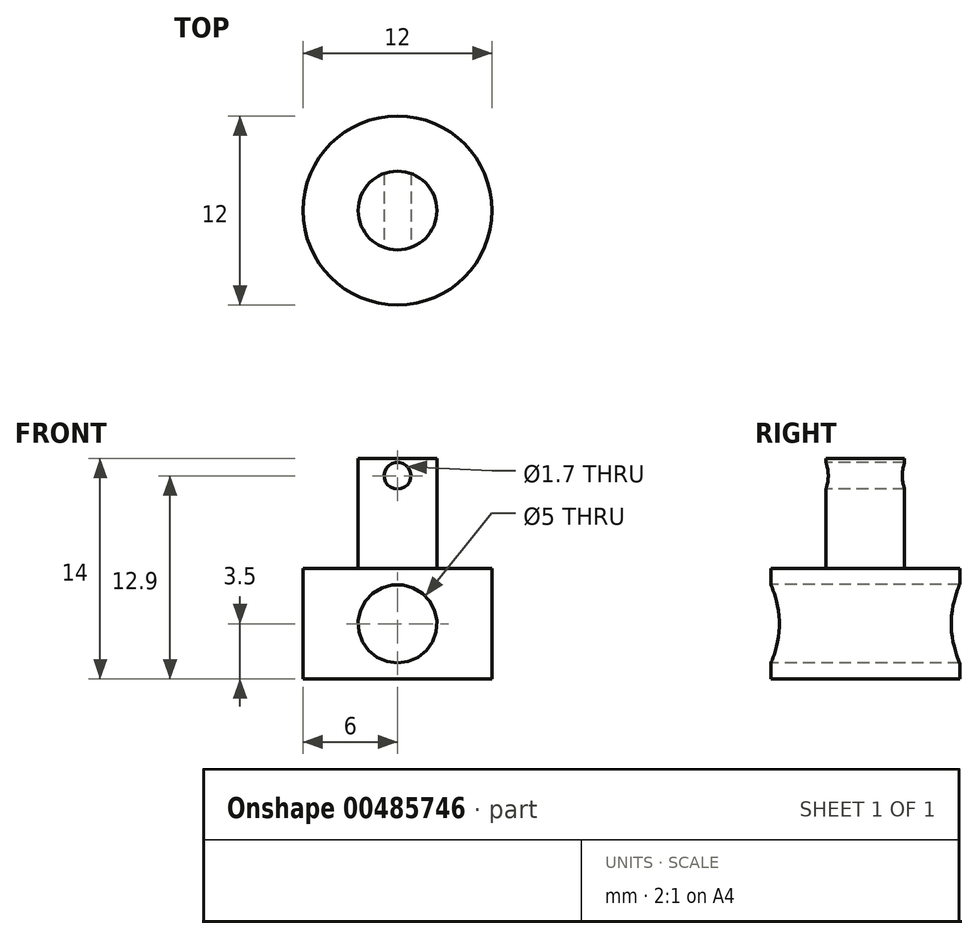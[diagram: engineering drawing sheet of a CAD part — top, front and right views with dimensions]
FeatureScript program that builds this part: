
annotation { "Feature Type Name" : "Feature", "Feature Type Description" : "" }
export const myFeature = defineFeature(function(context is Context, id is Id, definition is map)
    precondition{}
    {
        {
            var Q0;
            Q0=qCreatedBy(makeId("Front.planeOp"),FACE);
            var sketch = newSketch(context, id + "F0", { "sketchPlane" : qUnion([Q0]), "disableImprinting" : false});
            skLineSegment(sketch, "E0", {"start": v(0, 0) * mm, "end": v(6, 0) * mm});
            skLineSegment(sketch, "E1", {"start": v(6, 0) * mm, "end": v(6, 7) * mm});
            skLineSegment(sketch, "E2", {"start": v(6, 7) * mm, "end": v(2.5, 7) * mm});
            skLineSegment(sketch, "E3", {"start": v(2.5, 7) * mm, "end": v(2.5, 14) * mm});
            skLineSegment(sketch, "E4", {"start": v(2.5, 14) * mm, "end": v(0, 14) * mm});
            skLineSegment(sketch, "E5", {"start": v(0, 14) * mm, "end": v(0, 0) * mm});
            skLineSegment(sketch, "E6", {"start": v(0, 8.6) * mm, "end": v(0, 14) * mm, "construction": true});
            skSolve(sketch);
        }
        {
            var Q0;
            Q0=makeQuery(id+"F0.imprint","IMPRINT",FACE,{"disambiguationData":[TD([[makeQuery(id+"F0.imprint","IMPRINT",EDGE,{"derivedFrom":sQuery(id+"F0.wireOp",EDGE,"E0")}),1.0]])]});
            var Q1;
            Q1=sQuery(id+"F0.wireOp",EDGE,"E5");
            revolve(context, id + "F1", {"entities" : qUnion([Q0]), "axis" : qUnion([Q1]), "revolveType" : RevolveType.FULL});
        }
        {
            var Q0;
            Q0=qCreatedBy(makeId("Front.planeOp"),FACE);
            var sketch = newSketch(context, id + "F2", { "sketchPlane" : qUnion([Q0])});
            skCircle(sketch, "E7", {"center": v(0, 3.5) * mm, "radius": 2.5 * mm});
            skCircle(sketch, "E8", {"center": v(0, 12.9) * mm, "radius": 0.85 * mm});
            skSolve(sketch);
        }
        {
            var Q0;
            Q0 = qSketchRegion(id + "F2", true);
            extrude(context, id + "F3", {"entities" : qUnion([Q0]), "operationType" : NewBodyOperationType.REMOVE, "endBound" : BoundingType.THROUGH_ALL, "oppositeDirection" : true, "depth" : 25 * mm, "offsetDistance" : 25 * mm, "hasSecondDirection" : true, "secondDirectionBound" : BoundingType.THROUGH_ALL, "secondDirectionOppositeDirection" : false, "secondDirectionDepth" : 25 * mm});
        }
    });
